# Revit family: LCAT-G
name_source: partatom
category: Lighting Fixtures
revit_build: Autodesk Revit 2013 (Build: 20120221_2030(x64)
units: mm (PartAtom-declared; Revit-internal decimal feet)

## types (4) — shared parameters
Backbox = Hubbell - White
Certifications = UL1598 & CSA
Color Filter = 16777215
Default Elevation = 48 "
Description = Center-Lens Troffer
Dimming = 0-10V
Dimming Lamp Color Temperature Shift = <None>
Emit Shape Visible in Rendering = No
Emit from Rectangle Width = 22 "
Lamp = LED lamp
Light Bulb = Hubbell - White Glass
Load Classification = Lighting
Manufacturer = Columbia Lighting
Manufacturer Fax = (866)-898-1065
Mounting = Recessed mount
Photometric Web File = generic
Power Factor = 1
Product Documentation Link = http://cdn.columbialighting.com
Product Page URL = http://www.columbialighting.com
Tilt Angle = 90.00°
URL = http://www.columbialighting.com
Voltage = 120 V
Warranty = Five-year warranty
Wattage Comments = 28.9W-43.9W
Width = 24 "

## per-type parameters (varying)
| type | Apparent Load | Emit from Rectangle Length | Model | Row Length | Watts | zz Length |
| CCL24-5035 | 44 VA | 46 " | CCL24 | 48 " | 44 W | 47 " |
| CCL22-3335 | 29 VA | 22 " | CCL22 | 24 " | 29 W | 23 " |
| CCL22-3340 | 29 VA | 22 " | CCL22 | 24 " | 29 W | 23 " |
| CCL24-5040 | 44 VA | 46 " | CCL24 | 48 " | 44 W | 47 " |

## geometry (parser evidence)
native form markers: Sweep x4
no freeform markers — native parametric forms only
